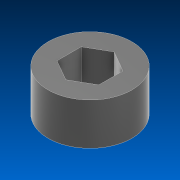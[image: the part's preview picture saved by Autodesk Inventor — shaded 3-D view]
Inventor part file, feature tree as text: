
AUTODESK INVENTOR PART (.ipt)
format: ipt  version: 2022.2 (Build 262287000, 287)  size: 93,184 bytes
history: native  units: in
note: dims shown in document units (in); Inventor stores cm internally (conversion verified against a paired STEP export)
features: extrude x1, sketch x1
ambient origin geometry x8: Origin, YZ Plane, XZ Plane, XY Plane, X Axis, Y Axis, Z Axis, Center Point
bodies: Solid1 (feature_tree)
feature tree (2):
  extrude  "Extrusion1"  Depth=0.25in
  sketch  "Sketch1"  dims[d0=0.25in d1=0.5in d2=0.25in d3=0.0in]
